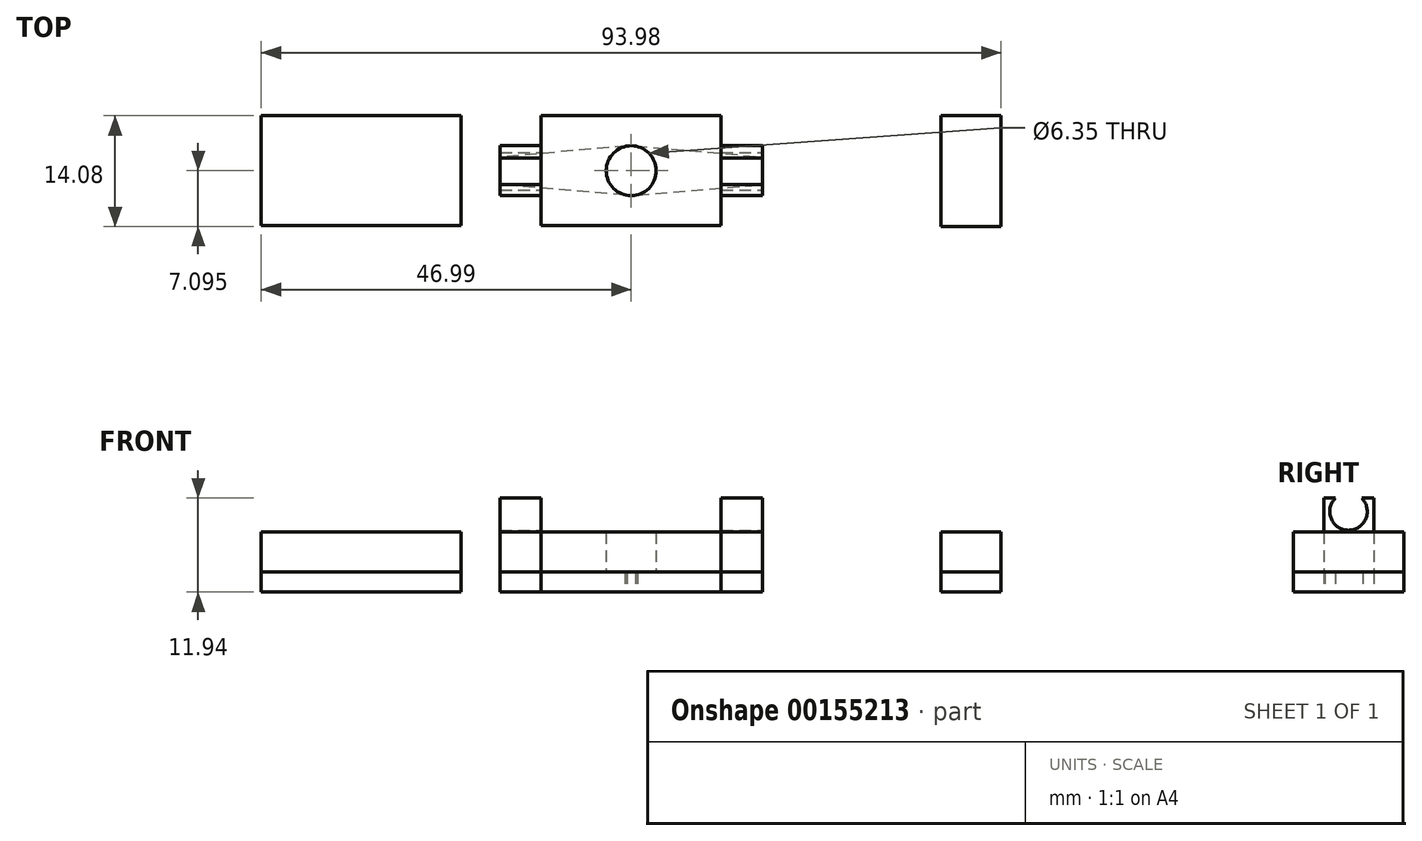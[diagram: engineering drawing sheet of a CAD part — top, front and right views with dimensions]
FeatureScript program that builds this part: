
annotation { "Feature Type Name" : "Feature", "Feature Type Description" : "" }
export const myFeature = defineFeature(function(context is Context, id is Id, definition is map)
    precondition{}
    {
        {
            var Q0;
            Q0=qCreatedBy(makeId("Top.planeOp"),FACE);
            var sketch = newSketch(context, id + "F0", { "sketchPlane" : qUnion([Q0])});
            skLineSegment(sketch, "E0.bottom", {"start": v(-21.08, -13.97) * mm, "end": v(22.1, -13.97) * mm});
            skLineSegment(sketch, "E0.top", {"start": v(-21.08, 0) * mm, "end": v(22.1, 0) * mm});
            skLineSegment(sketch, "E0.left", {"start": v(-21.08, -13.97) * mm, "end": v(-21.08, 0) * mm});
            skLineSegment(sketch, "E0.right", {"start": v(22.1, -13.97) * mm, "end": v(22.1, 0) * mm});
            skLineSegment(sketch, "E1.bottom", {"start": v(-16.16, -10.16) * mm, "end": v(17.18, -10.16) * mm});
            skLineSegment(sketch, "E1.top", {"start": v(-16.16, -3.81) * mm, "end": v(17.18, -3.81) * mm});
            skLineSegment(sketch, "E1.left", {"start": v(-16.16, -10.16) * mm, "end": v(-16.16, -3.81) * mm});
            skLineSegment(sketch, "E1.right", {"start": v(17.18, -10.16) * mm, "end": v(17.18, -3.81) * mm});
            skCircle(sketch, "E2", {"center": v(0.51, -6.99) * mm, "radius": 3.18 * mm});
            skLineSegment(sketch, "E3", {"start": v(0.51, -3.81) * mm, "end": v(-16.16, -5.25) * mm});
            skLineSegment(sketch, "E4", {"start": v(0.51, -10.13) * mm, "end": v(17.18, -8.74) * mm});
            skPoint(sketch, "E4.startSnap0", {"position": v(0.51, -10.16) * mm});
            skLineSegment(sketch, "E5", {"start": v(0.51, -3.81) * mm, "end": v(17.18, -5.23) * mm});
            skLineSegment(sketch, "E6", {"start": v(0.51, -10.13) * mm, "end": v(-16.16, -8.74) * mm});
            skLineSegment(sketch, "E7.bottom", {"start": v(-10.92, -13.97) * mm, "end": v(-21.08, -13.97) * mm});
            skLineSegment(sketch, "E7.top", {"start": v(-10.92, 0) * mm, "end": v(-21.08, 0) * mm});
            skLineSegment(sketch, "E7.left", {"start": v(-10.92, -13.97) * mm, "end": v(-10.92, 0) * mm});
            skLineSegment(sketch, "E8.bottom", {"start": v(22.1, -13.97) * mm, "end": v(11.94, -13.97) * mm});
            skLineSegment(sketch, "E8.top", {"start": v(22.1, 0) * mm, "end": v(11.94, 0) * mm});
            skLineSegment(sketch, "E8.right", {"start": v(11.94, -13.97) * mm, "end": v(11.94, 0) * mm});
            skLineSegment(sketch, "E9.bottom", {"start": v(-21.08, -13.97) * mm, "end": v(-21.08, -13.97) * mm});
            skLineSegment(sketch, "E9.top", {"start": v(-21.08, 0) * mm, "end": v(-21.08, 0) * mm});
            skLineSegment(sketch, "E10.bottom", {"start": v(-21.08, -13.97) * mm, "end": v(-46.48, -13.97) * mm});
            skLineSegment(sketch, "E10.top", {"start": v(-21.08, 0) * mm, "end": v(-46.48, 0) * mm});
            skLineSegment(sketch, "E10.right", {"start": v(-46.48, -13.97) * mm, "end": v(-46.48, 0) * mm});
            skLineSegment(sketch, "E11.bottom", {"start": v(22.1, 0) * mm, "end": v(47.5, 0) * mm});
            skLineSegment(sketch, "E11.top", {"start": v(22.1, -14.08) * mm, "end": v(47.5, -14.08) * mm});
            skLineSegment(sketch, "E11.left", {"start": v(22.1, 0) * mm, "end": v(22.1, -14.08) * mm});
            skLineSegment(sketch, "E11.right", {"start": v(47.5, 0) * mm, "end": v(47.5, -14.08) * mm});
            skLineSegment(sketch, "E12.bottom", {"start": v(47.5, -14.08) * mm, "end": v(39.88, -14.08) * mm});
            skLineSegment(sketch, "E12.top", {"start": v(47.5, 0) * mm, "end": v(39.88, 0) * mm});
            skLineSegment(sketch, "E12.left", {"start": v(47.5, -14.08) * mm, "end": v(47.5, 0) * mm});
            skLineSegment(sketch, "E12.right", {"start": v(39.88, -14.08) * mm, "end": v(39.88, 0) * mm});
            skLineSegment(sketch, "E13.bottom", {"start": v(-46.48, 0) * mm, "end": v(-38.86, 0) * mm});
            skLineSegment(sketch, "E13.top", {"start": v(-46.48, -13.97) * mm, "end": v(-38.86, -13.97) * mm});
            skLineSegment(sketch, "E13.left", {"start": v(-46.48, 0) * mm, "end": v(-46.48, -13.97) * mm});
            skLineSegment(sketch, "E13.right", {"start": v(-38.86, 0) * mm, "end": v(-38.86, -13.97) * mm});
            skSolve(sketch);
        }
        {
            var Q0;
            {var subQ5=sQuery(id+"F0.wireOp",EDGE,"E0.bottom");Q0=makeQuery(id+"F0.imprint","IMPRINT",FACE,{"disambiguationData":[TD([[makeQuery(id+"F0.imprint","IMPRINT",EDGE,{"derivedFrom":subQ5}),1.0]])]});}
            var Q1;
            {var subQ0=sQuery(id+"F0.wireOp",EDGE,"E1.right");var subQ1=sQuery(id+"F0.wireOp",EDGE,"E1.top");var subQ2=makeQuery(id+"F0.imprint","INTERSECT",VERTEX,{"derivedFrom":[subQ1,subQ0]});Q1=makeQuery(id+"F0.imprint","IMPRINT",FACE,{"disambiguationData":[TD([[makeQuery(id+"F0.imprint","IMPRINT",EDGE,{"disambiguationData":[TD([[subQ2,1.0]])],"derivedFrom":subQ1}),-1.0]])]});}
            var Q2;
            {var subQ0=sQuery(id+"F0.wireOp",EDGE,"E1.right");var subQ1=sQuery(id+"F0.wireOp",EDGE,"E1.bottom");var subQ2=makeQuery(id+"F0.imprint","INTERSECT",VERTEX,{"derivedFrom":[subQ1,subQ0]});Q2=makeQuery(id+"F0.imprint","IMPRINT",FACE,{"disambiguationData":[TD([[makeQuery(id+"F0.imprint","IMPRINT",EDGE,{"disambiguationData":[TD([[subQ2,1.0]])],"derivedFrom":subQ1}),1.0]])]});}
            var Q3;
            {var subQ6=sQuery(id+"F0.wireOp",EDGE,"E7.bottom");Q3=makeQuery(id+"F0.imprint","IMPRINT",FACE,{"disambiguationData":[TD([[makeQuery(id+"F0.imprint","IMPRINT",EDGE,{"derivedFrom":subQ6}),-1.0]])]});}
            var Q4;
            {var subQ0=sQuery(id+"F0.wireOp",EDGE,"E1.left");var subQ1=sQuery(id+"F0.wireOp",EDGE,"E1.bottom");var subQ2=makeQuery(id+"F0.imprint","INTERSECT",VERTEX,{"derivedFrom":[subQ1,subQ0]});Q4=makeQuery(id+"F0.imprint","IMPRINT",FACE,{"disambiguationData":[TD([[makeQuery(id+"F0.imprint","IMPRINT",EDGE,{"disambiguationData":[TD([[subQ2,-1.0]])],"derivedFrom":subQ1}),1.0]])]});}
            var Q5;
            {var subQ0=sQuery(id+"F0.wireOp",EDGE,"E1.left");var subQ1=sQuery(id+"F0.wireOp",EDGE,"E1.top");var subQ2=makeQuery(id+"F0.imprint","INTERSECT",VERTEX,{"derivedFrom":[subQ1,subQ0]});Q5=makeQuery(id+"F0.imprint","IMPRINT",FACE,{"disambiguationData":[TD([[makeQuery(id+"F0.imprint","IMPRINT",EDGE,{"disambiguationData":[TD([[subQ2,-1.0]])],"derivedFrom":subQ1}),-1.0]])]});}
            var Q6;
            {var subQ0=sQuery(id+"F0.wireOp",EDGE,"E7.left");var subQ1=sQuery(id+"F0.wireOp",EDGE,"E1.bottom");var subQ2=makeQuery(id+"F0.imprint","INTERSECT",VERTEX,{"derivedFrom":[subQ1,subQ0]});Q6=makeQuery(id+"F0.imprint","IMPRINT",FACE,{"disambiguationData":[TD([[makeQuery(id+"F0.imprint","IMPRINT",EDGE,{"disambiguationData":[TD([[subQ2,-1.0]])],"derivedFrom":subQ1}),1.0]])]});}
            var Q7;
            {var subQ5=sQuery(id+"F0.wireOp",EDGE,"E0.top");Q7=makeQuery(id+"F0.imprint","IMPRINT",FACE,{"disambiguationData":[TD([[makeQuery(id+"F0.imprint","IMPRINT",EDGE,{"derivedFrom":subQ5}),-1.0]])]});}
            var Q8;
            {var subQ0=sQuery(id+"F0.wireOp",EDGE,"E5");var subQ1=sQuery(id+"F0.wireOp",EDGE,"E2");var subQ6=makeQuery(id+"F0.imprint","INTERSECT",VERTEX,{"derivedFrom":[subQ1,subQ0]});Q8=makeQuery(id+"F0.imprint","IMPRINT",FACE,{"disambiguationData":[TD([[makeQuery(id+"F0.imprint","IMPRINT",EDGE,{"disambiguationData":[TD([[subQ6,-1.0]])],"derivedFrom":subQ0}),1.0]])]});}
            var Q9;
            {var subQ11=sQuery(id+"F0.wireOp",EDGE,"E8.bottom");Q9=makeQuery(id+"F0.imprint","IMPRINT",FACE,{"disambiguationData":[TD([[makeQuery(id+"F0.imprint","IMPRINT",EDGE,{"derivedFrom":subQ11}),-1.0]])]});}
            var Q10;
            {var subQ0=sQuery(id+"F0.wireOp",EDGE,"E2");var subQ1=sQuery(id+"F0.wireOp",EDGE,"E1.bottom");var subQ2=makeQuery(id+"F0.imprint","INTERSECT",VERTEX,{"derivedFrom":[subQ1,subQ0]});Q10=makeQuery(id+"F0.imprint","IMPRINT",FACE,{"disambiguationData":[TD([[makeQuery(id+"F0.imprint","IMPRINT",EDGE,{"disambiguationData":[TD([[subQ2,-1.0]])],"derivedFrom":subQ1}),1.0]])]});}
            var Q11;
            {var subQ0=sQuery(id+"F0.wireOp",EDGE,"E3");var subQ1=sQuery(id+"F0.wireOp",EDGE,"E2");var subQ6=makeQuery(id+"F0.imprint","INTERSECT",VERTEX,{"derivedFrom":[subQ1,subQ0]});Q11=makeQuery(id+"F0.imprint","IMPRINT",FACE,{"disambiguationData":[TD([[makeQuery(id+"F0.imprint","IMPRINT",EDGE,{"disambiguationData":[TD([[subQ6,-1.0]])],"derivedFrom":subQ0}),-1.0]])]});}
            var Q12;
            Q12=makeQuery(id+"F0.imprint","IMPRINT",FACE,{"disambiguationData":[TD([[makeQuery(id+"F0.imprint","IMPRINT",EDGE,{"derivedFrom":sQuery(id+"F0.wireOp",EDGE,"E10.bottom")}),-1.0]])]});
            var Q13;
            {var subQ3=sQuery(id+"F0.wireOp",EDGE,"E11.bottom");Q13=makeQuery(id+"F0.imprint","IMPRINT",FACE,{"disambiguationData":[TD([[makeQuery(id+"F0.imprint","IMPRINT",EDGE,{"derivedFrom":subQ3}),-1.0]])]});}
            extrude(context, id + "F1", {"entities" : qUnion([Q0, Q1, Q2, Q3, Q4, Q5, Q6, Q7, Q8, Q9, Q10, Q11, Q12, Q13]), "depth" : 2.54 * mm});
        }
        {
            var Q0;
            {var subQ0=sQuery(id+"F0.wireOp",EDGE,"E1.right");var subQ1=sQuery(id+"F0.wireOp",EDGE,"E1.bottom");var subQ2=makeQuery(id+"F0.imprint","INTERSECT",VERTEX,{"derivedFrom":[subQ1,subQ0]});Q0=makeQuery(id+"F0.imprint","IMPRINT",FACE,{"disambiguationData":[TD([[makeQuery(id+"F0.imprint","IMPRINT",EDGE,{"disambiguationData":[TD([[subQ2,1.0]])],"derivedFrom":subQ1}),1.0]])]});}
            var Q1;
            {var subQ0=sQuery(id+"F0.wireOp",EDGE,"E4");var subQ1=sQuery(id+"F0.wireOp",EDGE,"E1.right");var subQ2=makeQuery(id+"F0.imprint","INTERSECT",VERTEX,{"derivedFrom":[subQ1,subQ0]});Q1=makeQuery(id+"F0.imprint","IMPRINT",FACE,{"disambiguationData":[TD([[makeQuery(id+"F0.imprint","IMPRINT",EDGE,{"disambiguationData":[TD([[subQ2,-1.0]])],"derivedFrom":subQ1}),1.0]])]});}
            var Q2;
            {var subQ0=sQuery(id+"F0.wireOp",EDGE,"E1.right");var subQ1=sQuery(id+"F0.wireOp",EDGE,"E1.top");var subQ2=makeQuery(id+"F0.imprint","INTERSECT",VERTEX,{"derivedFrom":[subQ1,subQ0]});Q2=makeQuery(id+"F0.imprint","IMPRINT",FACE,{"disambiguationData":[TD([[makeQuery(id+"F0.imprint","IMPRINT",EDGE,{"disambiguationData":[TD([[subQ2,1.0]])],"derivedFrom":subQ0}),1.0]])]});}
            var Q3;
            {var subQ0=sQuery(id+"F0.wireOp",EDGE,"E1.left");var subQ1=sQuery(id+"F0.wireOp",EDGE,"E1.bottom");var subQ2=makeQuery(id+"F0.imprint","INTERSECT",VERTEX,{"derivedFrom":[subQ1,subQ0]});Q3=makeQuery(id+"F0.imprint","IMPRINT",FACE,{"disambiguationData":[TD([[makeQuery(id+"F0.imprint","IMPRINT",EDGE,{"disambiguationData":[TD([[subQ2,-1.0]])],"derivedFrom":subQ1}),1.0]])]});}
            var Q4;
            {var subQ0=sQuery(id+"F0.wireOp",EDGE,"E1.left");var subQ1=sQuery(id+"F0.wireOp",EDGE,"E1.top");var subQ2=makeQuery(id+"F0.imprint","INTERSECT",VERTEX,{"derivedFrom":[subQ1,subQ0]});Q4=makeQuery(id+"F0.imprint","IMPRINT",FACE,{"disambiguationData":[TD([[makeQuery(id+"F0.imprint","IMPRINT",EDGE,{"disambiguationData":[TD([[subQ2,1.0]])],"derivedFrom":subQ0}),-1.0]])]});}
            var Q5;
            {var subQ0=sQuery(id+"F0.wireOp",EDGE,"E3");var subQ1=sQuery(id+"F0.wireOp",EDGE,"E1.left");var subQ2=makeQuery(id+"F0.imprint","INTERSECT",VERTEX,{"derivedFrom":[subQ1,subQ0]});Q5=makeQuery(id+"F0.imprint","IMPRINT",FACE,{"disambiguationData":[TD([[makeQuery(id+"F0.imprint","IMPRINT",EDGE,{"disambiguationData":[TD([[subQ2,1.0]])],"derivedFrom":subQ1}),-1.0]])]});}
            var Q6;
            {var subQ0=sQuery(id+"F0.wireOp",EDGE,"E3");var subQ1=sQuery(id+"F0.wireOp",EDGE,"E2");var subQ2=makeQuery(id+"F0.imprint","INTERSECT",VERTEX,{"derivedFrom":[subQ1,subQ0]});Q6=makeQuery(id+"F0.imprint","IMPRINT",FACE,{"disambiguationData":[TD([[makeQuery(id+"F0.imprint","IMPRINT",EDGE,{"disambiguationData":[TD([[subQ2,-1.0]])],"derivedFrom":subQ1}),-1.0]])]});}
            var Q7;
            {var subQ6=sQuery(id+"F0.wireOp",EDGE,"E7.bottom");Q7=makeQuery(id+"F0.imprint","IMPRINT",FACE,{"disambiguationData":[TD([[makeQuery(id+"F0.imprint","IMPRINT",EDGE,{"derivedFrom":subQ6}),-1.0]])]});}
            var Q8;
            {var subQ0=sQuery(id+"F0.wireOp",EDGE,"E7.left");var subQ1=sQuery(id+"F0.wireOp",EDGE,"E1.bottom");var subQ2=makeQuery(id+"F0.imprint","INTERSECT",VERTEX,{"derivedFrom":[subQ1,subQ0]});Q8=makeQuery(id+"F0.imprint","IMPRINT",FACE,{"disambiguationData":[TD([[makeQuery(id+"F0.imprint","IMPRINT",EDGE,{"disambiguationData":[TD([[subQ2,-1.0]])],"derivedFrom":subQ1}),1.0]])]});}
            var Q9;
            {var subQ11=sQuery(id+"F0.wireOp",EDGE,"E8.bottom");Q9=makeQuery(id+"F0.imprint","IMPRINT",FACE,{"disambiguationData":[TD([[makeQuery(id+"F0.imprint","IMPRINT",EDGE,{"derivedFrom":subQ11}),-1.0]])]});}
            var Q10;
            {var subQ0=sQuery(id+"F0.wireOp",EDGE,"E5");var subQ1=sQuery(id+"F0.wireOp",EDGE,"E2");var subQ2=makeQuery(id+"F0.imprint","INTERSECT",VERTEX,{"derivedFrom":[subQ1,subQ0]});Q10=makeQuery(id+"F0.imprint","IMPRINT",FACE,{"disambiguationData":[TD([[makeQuery(id+"F0.imprint","IMPRINT",EDGE,{"disambiguationData":[TD([[subQ2,1.0]])],"derivedFrom":subQ1}),-1.0]])]});}
            var Q11;
            {var subQ5=sQuery(id+"F0.wireOp",EDGE,"E0.top");Q11=makeQuery(id+"F0.imprint","IMPRINT",FACE,{"disambiguationData":[TD([[makeQuery(id+"F0.imprint","IMPRINT",EDGE,{"derivedFrom":subQ5}),-1.0]])]});}
            var Q12;
            {var subQ5=sQuery(id+"F0.wireOp",EDGE,"E0.bottom");Q12=makeQuery(id+"F0.imprint","IMPRINT",FACE,{"disambiguationData":[TD([[makeQuery(id+"F0.imprint","IMPRINT",EDGE,{"derivedFrom":subQ5}),1.0]])]});}
            var Q13;
            {var subQ0=sQuery(id+"F0.wireOp",EDGE,"E2");var subQ1=sQuery(id+"F0.wireOp",EDGE,"E1.bottom");var subQ2=makeQuery(id+"F0.imprint","INTERSECT",VERTEX,{"derivedFrom":[subQ1,subQ0]});Q13=makeQuery(id+"F0.imprint","IMPRINT",FACE,{"disambiguationData":[TD([[makeQuery(id+"F0.imprint","IMPRINT",EDGE,{"disambiguationData":[TD([[subQ2,-1.0]])],"derivedFrom":subQ1}),1.0]])]});}
            var Q14;
            {var subQ0=sQuery(id+"F0.wireOp",EDGE,"E5");var subQ1=sQuery(id+"F0.wireOp",EDGE,"E2");var subQ6=makeQuery(id+"F0.imprint","INTERSECT",VERTEX,{"derivedFrom":[subQ1,subQ0]});Q14=makeQuery(id+"F0.imprint","IMPRINT",FACE,{"disambiguationData":[TD([[makeQuery(id+"F0.imprint","IMPRINT",EDGE,{"disambiguationData":[TD([[subQ6,-1.0]])],"derivedFrom":subQ0}),1.0]])]});}
            var Q15;
            {var subQ0=sQuery(id+"F0.wireOp",EDGE,"E3");var subQ1=sQuery(id+"F0.wireOp",EDGE,"E2");var subQ6=makeQuery(id+"F0.imprint","INTERSECT",VERTEX,{"derivedFrom":[subQ1,subQ0]});Q15=makeQuery(id+"F0.imprint","IMPRINT",FACE,{"disambiguationData":[TD([[makeQuery(id+"F0.imprint","IMPRINT",EDGE,{"disambiguationData":[TD([[subQ6,-1.0]])],"derivedFrom":subQ0}),-1.0]])]});}
            var Q16;
            Q16=makeQuery(id+"F0.imprint","IMPRINT",FACE,{"disambiguationData":[TD([[makeQuery(id+"F0.imprint","IMPRINT",EDGE,{"derivedFrom":sQuery(id+"F0.wireOp",EDGE,"E10.bottom")}),-1.0]])]});
            var Q17;
            {var subQ3=sQuery(id+"F0.wireOp",EDGE,"E11.bottom");Q17=makeQuery(id+"F0.imprint","IMPRINT",FACE,{"disambiguationData":[TD([[makeQuery(id+"F0.imprint","IMPRINT",EDGE,{"derivedFrom":subQ3}),-1.0]])]});}
            var Q18;
            Q18=makeQuery(id+"F0.imprint","IMPRINT",FACE,{"disambiguationData":[TD([[makeQuery(id+"F0.imprint","IMPRINT",EDGE,{"derivedFrom":sQuery(id+"F0.wireOp",EDGE,"E13.bottom")}),-1.0]])]});
            var Q19;
            Q19=makeQuery(id+"F0.imprint","IMPRINT",FACE,{"disambiguationData":[TD([[makeQuery(id+"F0.imprint","IMPRINT",EDGE,{"derivedFrom":sQuery(id+"F0.wireOp",EDGE,"E12.bottom")}),-1.0]])]});
            extrude(context, id + "F2", {"entities" : qUnion([Q0, Q1, Q2, Q3, Q4, Q5, Q6, Q7, Q8, Q9, Q10, Q11, Q12, Q13, Q14, Q15, Q16, Q17, Q18, Q19]), "depth" : 7.62 * mm, "hasSecondDirection" : true, "secondDirectionOppositeDirection" : false, "secondDirectionDepth" : 2.54 * mm});
        }
        {
            var Q0;
            {var subQ0=sQuery(id+"F0.wireOp",EDGE,"E1.left");var subQ1=sQuery(id+"F0.wireOp",EDGE,"E1.bottom");var subQ2=makeQuery(id+"F0.imprint","INTERSECT",VERTEX,{"derivedFrom":[subQ1,subQ0]});Q0=makeQuery(id+"F0.imprint","IMPRINT",FACE,{"disambiguationData":[TD([[makeQuery(id+"F0.imprint","IMPRINT",EDGE,{"disambiguationData":[TD([[subQ2,-1.0]])],"derivedFrom":subQ1}),1.0]])]});}
            var Q1;
            {var subQ0=sQuery(id+"F0.wireOp",EDGE,"E1.left");var subQ1=sQuery(id+"F0.wireOp",EDGE,"E1.top");var subQ2=makeQuery(id+"F0.imprint","INTERSECT",VERTEX,{"derivedFrom":[subQ1,subQ0]});Q1=makeQuery(id+"F0.imprint","IMPRINT",FACE,{"disambiguationData":[TD([[makeQuery(id+"F0.imprint","IMPRINT",EDGE,{"disambiguationData":[TD([[subQ2,-1.0]])],"derivedFrom":subQ1}),-1.0]])]});}
            var Q2;
            {var subQ0=sQuery(id+"F0.wireOp",EDGE,"E3");var subQ1=sQuery(id+"F0.wireOp",EDGE,"E1.left");var subQ2=makeQuery(id+"F0.imprint","INTERSECT",VERTEX,{"derivedFrom":[subQ1,subQ0]});Q2=makeQuery(id+"F0.imprint","IMPRINT",FACE,{"disambiguationData":[TD([[makeQuery(id+"F0.imprint","IMPRINT",EDGE,{"disambiguationData":[TD([[subQ2,1.0]])],"derivedFrom":subQ1}),-1.0]])]});}
            var Q3;
            {var subQ0=sQuery(id+"F0.wireOp",EDGE,"E1.right");var subQ1=sQuery(id+"F0.wireOp",EDGE,"E1.top");var subQ2=makeQuery(id+"F0.imprint","INTERSECT",VERTEX,{"derivedFrom":[subQ1,subQ0]});Q3=makeQuery(id+"F0.imprint","IMPRINT",FACE,{"disambiguationData":[TD([[makeQuery(id+"F0.imprint","IMPRINT",EDGE,{"disambiguationData":[TD([[subQ2,1.0]])],"derivedFrom":subQ1}),-1.0]])]});}
            var Q4;
            {var subQ0=sQuery(id+"F0.wireOp",EDGE,"E4");var subQ1=sQuery(id+"F0.wireOp",EDGE,"E1.right");var subQ2=makeQuery(id+"F0.imprint","INTERSECT",VERTEX,{"derivedFrom":[subQ1,subQ0]});Q4=makeQuery(id+"F0.imprint","IMPRINT",FACE,{"disambiguationData":[TD([[makeQuery(id+"F0.imprint","IMPRINT",EDGE,{"disambiguationData":[TD([[subQ2,-1.0]])],"derivedFrom":subQ1}),1.0]])]});}
            var Q5;
            {var subQ0=sQuery(id+"F0.wireOp",EDGE,"E1.right");var subQ1=sQuery(id+"F0.wireOp",EDGE,"E1.bottom");var subQ2=makeQuery(id+"F0.imprint","INTERSECT",VERTEX,{"derivedFrom":[subQ1,subQ0]});Q5=makeQuery(id+"F0.imprint","IMPRINT",FACE,{"disambiguationData":[TD([[makeQuery(id+"F0.imprint","IMPRINT",EDGE,{"disambiguationData":[TD([[subQ2,1.0]])],"derivedFrom":subQ1}),1.0]])]});}
            var Q6;
            Q6=makeQuery(id+"F0.imprint","IMPRINT",FACE,{"disambiguationData":[TD([[makeQuery(id+"F0.imprint","IMPRINT",EDGE,{"derivedFrom":sQuery(id+"F0.wireOp",EDGE,"E13.bottom")}),-1.0]])]});
            var Q7;
            Q7=makeQuery(id+"F0.imprint","IMPRINT",FACE,{"disambiguationData":[TD([[makeQuery(id+"F0.imprint","IMPRINT",EDGE,{"derivedFrom":sQuery(id+"F0.wireOp",EDGE,"E12.bottom")}),-1.0]])]});
            extrude(context, id + "F3", {"entities" : qUnion([Q0, Q1, Q2, Q3, Q4, Q5, Q6, Q7]), "depth" : 11.94 * mm, "hasSecondDirection" : true, "secondDirectionOppositeDirection" : false, "secondDirectionDepth" : 7.62 * mm});
        }
        {
            var Q0;
            Q0=qCreatedBy(makeId("Right.planeOp"),FACE);
            var sketch = newSketch(context, id + "F4", { "sketchPlane" : qUnion([Q0])});
            skCircle(sketch, "E14", {"center": v(-7.06, 10.25) * mm, "radius": 2.38 * mm});
            skSolve(sketch);
        }
        {
            var Q0;
            Q0=makeQuery(id+"F4.imprint","IMPRINT",FACE,{"disambiguationData":[TD([[makeQuery(id+"F4.imprint","IMPRINT",EDGE,{"derivedFrom":sQuery(id+"F4.wireOp",EDGE,"E14")}),1.0]])]});
            extrude(context, id + "F5", {"entities" : qUnion([Q0]), "operationType" : NewBodyOperationType.REMOVE, "oppositeDirection" : true, "depth" : 50.8 * mm, "hasSecondDirection" : true, "secondDirectionOppositeDirection" : false, "secondDirectionDepth" : 50.8 * mm});
        }
    });
